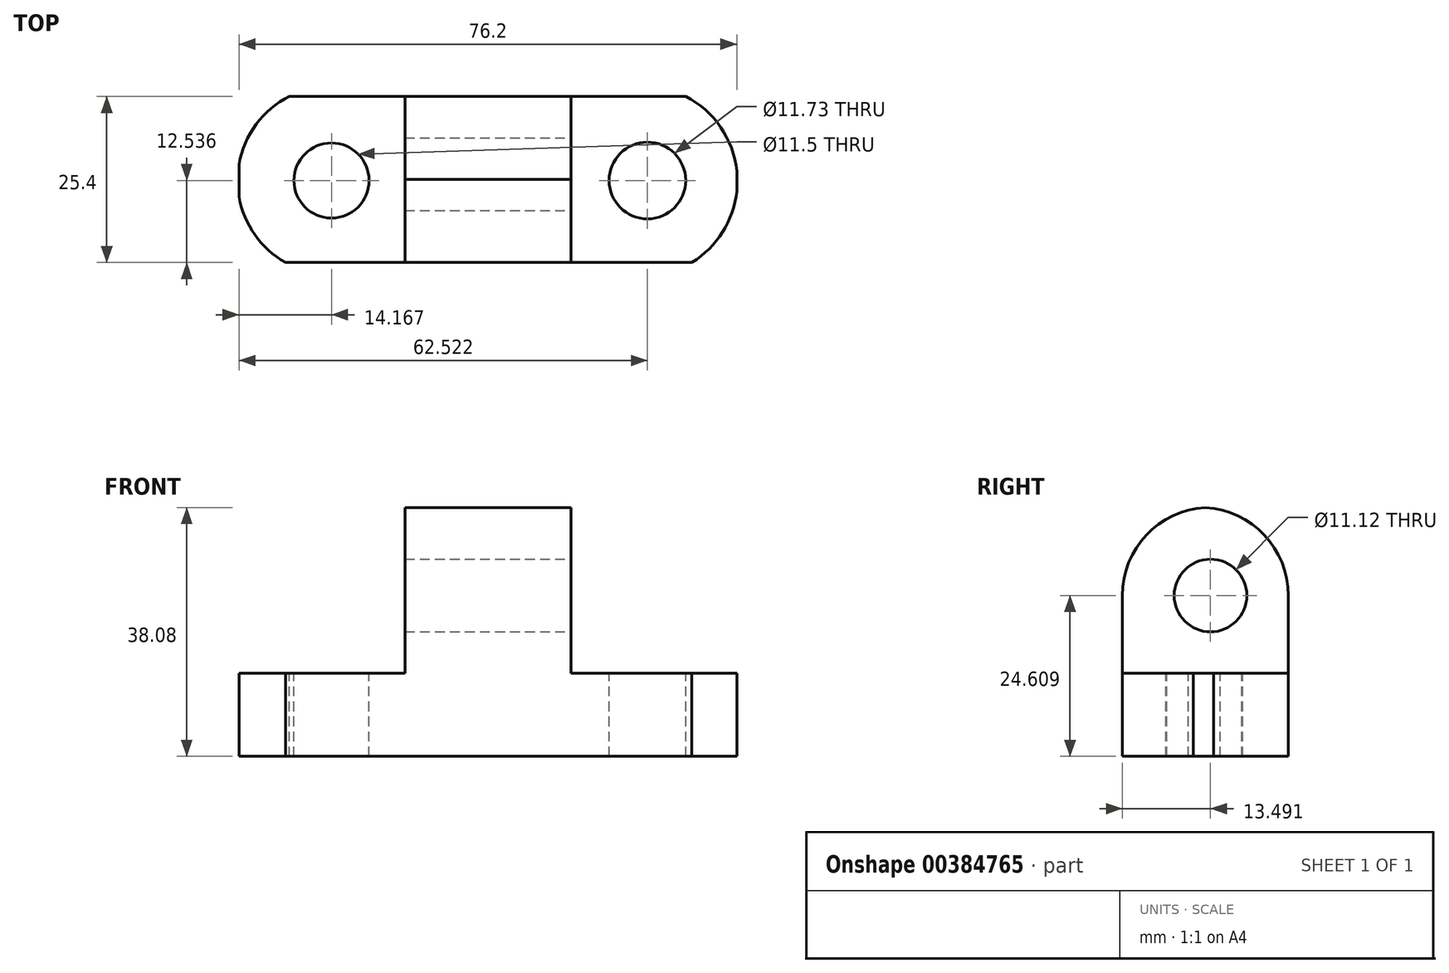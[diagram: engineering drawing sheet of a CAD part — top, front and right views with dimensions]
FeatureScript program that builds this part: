
annotation { "Feature Type Name" : "Feature", "Feature Type Description" : "" }
export const myFeature = defineFeature(function(context is Context, id is Id, definition is map)
    precondition{}
    {
        {
            var Q0;
            Q0=qCreatedBy(makeId("Front.planeOp"),FACE);
            var sketch = newSketch(context, id + "F0", { "sketchPlane" : qUnion([Q0])});
            skLineSegment(sketch, "E0", {"start": v(0, 12.7) * mm, "end": v(0, 0) * mm});
            skLineSegment(sketch, "E1", {"start": v(0, 0) * mm, "end": v(76.2, 0) * mm});
            skLineSegment(sketch, "E2", {"start": v(76.2, 0) * mm, "end": v(76.2, 12.7) * mm});
            skLineSegment(sketch, "E3", {"start": v(76.2, 12.7) * mm, "end": v(50.8, 12.7) * mm});
            skLineSegment(sketch, "E4", {"start": v(50.8, 12.7) * mm, "end": v(50.8, 38.1) * mm});
            skLineSegment(sketch, "E5", {"start": v(50.8, 38.1) * mm, "end": v(25.4, 38.1) * mm});
            skLineSegment(sketch, "E6", {"start": v(25.4, 38.1) * mm, "end": v(25.4, 12.7) * mm});
            skLineSegment(sketch, "E7", {"start": v(25.4, 12.7) * mm, "end": v(0, 12.7) * mm});
            skSolve(sketch);
        }
        {
            var Q0;
            Q0=makeQuery(id+"F0.imprint","IMPRINT",FACE,{"disambiguationData":[TD([[makeQuery(id+"F0.imprint","IMPRINT",EDGE,{"derivedFrom":sQuery(id+"F0.wireOp",EDGE,"E0")}),1.0]])]});
            extrude(context, id + "F1", {"entities" : qUnion([Q0]), "depth" : 25.4 * mm});
        }
        {
            var Q0;
            Q0=makeQuery(id+"F1.opExtrude","SWEPT_FACE",FACE,{"disambiguationData":[OSD([sQuery(id+"F0.wireOp",EDGE,"E7")])]});
            var sketch = newSketch(context, id + "F2", { "sketchPlane" : qUnion([Q0])});
            skArc(sketch, "E8", {"start": v(7.74, 0) * mm, "mid": v(-0.2, -12.51) * mm, "end": v(7.12, -25.4) * mm});
            skArc(sketch, "E9", {"start": v(70.26, -25.4) * mm, "mid": v(76.11, -12.1) * mm, "end": v(68.1, 0) * mm});
            skPoint(sketch, "E9.startSnap0", {"position": v(12.7, -25.4) * mm});
            skSolve(sketch);
        }
        {
            var Q0;
            {var subQ0=sQuery(id+"F2.wireOp",EDGE,"E8");var subQ1=sQuery(id+"F0.wireOp",EDGE,"E7");var subQ2=makeQuery(id+"F1.opExtrude","CAP_EDGE",EDGE,{"disambiguationData":[OSD([subQ1])],"isStart":true});var subQ3=makeQuery(id+"F2.imprint","INTERSECT",VERTEX,{"derivedFrom":[subQ2,subQ0]});Q0=makeQuery(id+"F2.imprint","IMPRINT",FACE,{"disambiguationData":[TD([[makeQuery(id+"F2.imprint","IMPRINT",EDGE,{"disambiguationData":[TD([[subQ3,-1.0]])],"derivedFrom":subQ0}),-1.0]])]});}
            var Q1;
            {var subQ0=sQuery(id+"F2.wireOp",EDGE,"E8");var subQ1=sQuery(id+"F0.wireOp",EDGE,"E7");var subQ2=makeQuery(id+"F1.opExtrude","CAP_EDGE",EDGE,{"disambiguationData":[OSD([subQ1])],"isStart":false});var subQ3=makeQuery(id+"F2.imprint","INTERSECT",VERTEX,{"derivedFrom":[subQ2,subQ0]});Q1=makeQuery(id+"F2.imprint","IMPRINT",FACE,{"disambiguationData":[TD([[makeQuery(id+"F2.imprint","IMPRINT",EDGE,{"disambiguationData":[TD([[subQ3,1.0]])],"derivedFrom":subQ0}),-1.0]])]});}
            extrude(context, id + "F3", {"entities" : qUnion([Q0, Q1]), "operationType" : NewBodyOperationType.REMOVE, "oppositeDirection" : true, "depth" : 25.4 * mm});
        }
        {
            var Q0;
            Q0=makeQuery(id+"F1.opExtrude","SWEPT_FACE",FACE,{"disambiguationData":[OSD([sQuery(id+"F0.wireOp",EDGE,"E3")])]});
            var sketch = newSketch(context, id + "F4", { "sketchPlane" : qUnion([Q0])});
            skArc(sketch, "E10", {"start": v(69.33, -25.4) * mm, "mid": v(76.27, -12.43) * mm, "end": v(68.4, 0) * mm});
            skLineSegment(sketch, "E11", {"start": v(68.4, 0) * mm, "end": v(76.2, 0) * mm});
            skLineSegment(sketch, "E12", {"start": v(76.2, 0) * mm, "end": v(76.2, -25.4) * mm});
            skLineSegment(sketch, "E13", {"start": v(76.2, -25.4) * mm, "end": v(69.33, -25.4) * mm});
            skSolve(sketch);
        }
        {
            var Q0;
            {var subQ0=sQuery(id+"F4.wireOp",EDGE,"E11");Q0=makeQuery(id+"F4.imprint","IMPRINT",FACE,{"disambiguationData":[TD([[makeQuery(id+"F4.imprint","IMPRINT",EDGE,{"derivedFrom":subQ0}),1.0]])]});}
            var Q1;
            {var subQ0=sQuery(id+"F4.wireOp",EDGE,"E13");Q1=makeQuery(id+"F4.imprint","IMPRINT",FACE,{"disambiguationData":[TD([[makeQuery(id+"F4.imprint","IMPRINT",EDGE,{"derivedFrom":subQ0}),-1.0]])]});}
            extrude(context, id + "F5", {"entities" : qUnion([Q0, Q1]), "operationType" : NewBodyOperationType.REMOVE, "oppositeDirection" : true, "depth" : 25.4 * mm});
        }
        {
            var Q0;
            Q0=makeQuery(id+"F1.opExtrude","CAP_EDGE",EDGE,{"disambiguationData":[OSD([sQuery(id+"F0.wireOp",EDGE,"E5")])],"isStart":false});
            var Q1;
            Q1=makeQuery(id+"F1.opExtrude","CAP_EDGE",EDGE,{"disambiguationData":[OSD([sQuery(id+"F0.wireOp",EDGE,"E5")])],"isStart":true});
            fillet(context, id + "F6", {"entities" : qUnion([Q0, Q1]), "radius" : 13.5 * mm, "tangentPropagation" : true, "allowEdgeOverflow" : false});
        }
        {
            var Q0;
            Q0=makeQuery(id+"F1.opExtrude","SWEPT_FACE",FACE,{"disambiguationData":[OSD([sQuery(id+"F0.wireOp",EDGE,"E4")])]});
            var sketch = newSketch(context, id + "F7", { "sketchPlane" : qUnion([Q0])});
            skCircle(sketch, "E14", {"center": v(-11.9, 24.6) * mm, "radius": 5.56 * mm});
            skSolve(sketch);
        }
        {
            var Q0;
            Q0=makeQuery(id+"F7.imprint","IMPRINT",FACE,{"disambiguationData":[TD([[makeQuery(id+"F7.imprint","IMPRINT",EDGE,{"derivedFrom":sQuery(id+"F7.wireOp",EDGE,"E14")}),1.0]])]});
            extrude(context, id + "F8", {"entities" : qUnion([Q0]), "operationType" : NewBodyOperationType.REMOVE, "oppositeDirection" : true, "depth" : 25.4 * mm});
        }
        {
            var Q0;
            Q0=makeQuery(id+"F1.opExtrude","SWEPT_FACE",FACE,{"disambiguationData":[OSD([sQuery(id+"F0.wireOp",EDGE,"E7")])]});
            var sketch = newSketch(context, id + "F9", { "sketchPlane" : qUnion([Q0])});
            skCircle(sketch, "E15", {"center": v(14.17, -12.86) * mm, "radius": 5.75 * mm});
            skCircle(sketch, "E16", {"center": v(62.52, -12.86) * mm, "radius": 5.87 * mm});
            skSolve(sketch);
        }
        {
            var Q0;
            Q0=makeQuery(id+"F9.imprint","IMPRINT",FACE,{"disambiguationData":[TD([[makeQuery(id+"F9.imprint","IMPRINT",EDGE,{"derivedFrom":sQuery(id+"F9.wireOp",EDGE,"E16")}),1.0]])]});
            extrude(context, id + "F10", {"entities" : qUnion([Q0]), "operationType" : NewBodyOperationType.REMOVE, "oppositeDirection" : true, "depth" : 25.4 * mm});
        }
        {
            var Q0;
            Q0=makeQuery(id+"F9.imprint","IMPRINT",FACE,{"disambiguationData":[TD([[makeQuery(id+"F9.imprint","IMPRINT",EDGE,{"derivedFrom":sQuery(id+"F9.wireOp",EDGE,"E15")}),1.0]])]});
            extrude(context, id + "F11", {"entities" : qUnion([Q0]), "operationType" : NewBodyOperationType.REMOVE, "oppositeDirection" : true, "depth" : 25.4 * mm});
        }
    });
